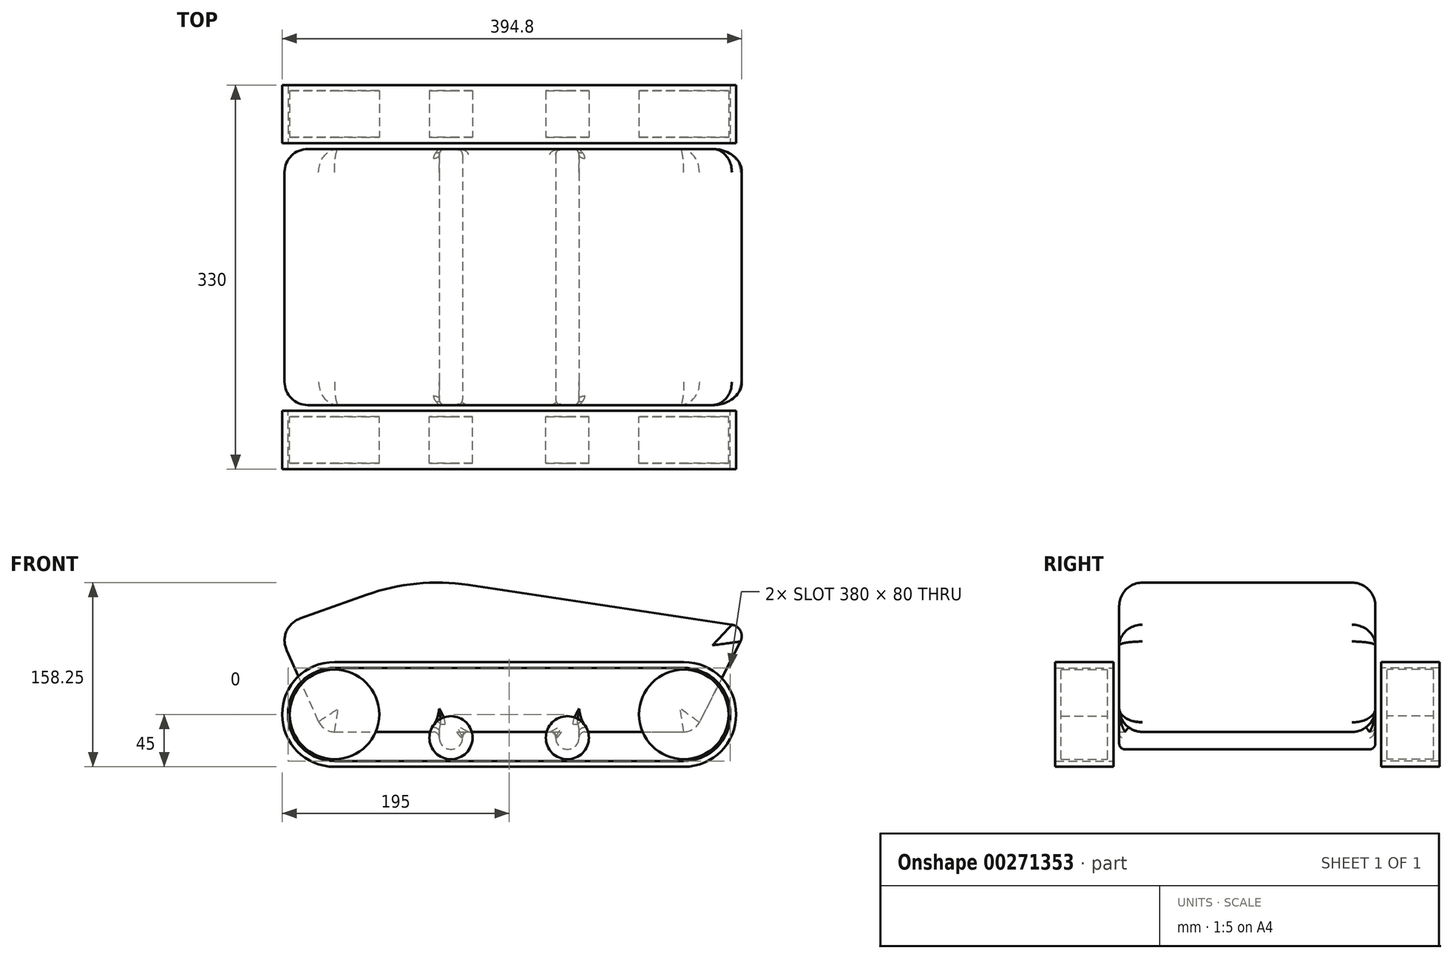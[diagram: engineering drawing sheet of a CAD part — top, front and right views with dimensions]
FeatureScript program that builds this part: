
annotation { "Feature Type Name" : "Feature", "Feature Type Description" : "" }
export const myFeature = defineFeature(function(context is Context, id is Id, definition is map)
    precondition{}
    {
        {
            var Q0;
            Q0=qCreatedBy(makeId("Front.planeOp"),FACE);
            var sketch = newSketch(context, id + "F0", { "sketchPlane" : qUnion([Q0])});
            skCircle(sketch, "E0", {"center": v(-150, 0) * mm, "radius": 40 * mm, "construction": true});
            skCircle(sketch, "E1", {"center": v(150, 0) * mm, "radius": 40 * mm, "construction": true});
            skCircle(sketch, "E2", {"center": v(-50, -20) * mm, "radius": 20 * mm, "construction": true});
            skCircle(sketch, "E3", {"center": v(50, -20) * mm, "radius": 20 * mm, "construction": true});
            skLineSegment(sketch, "E4", {"start": v(-150, -40) * mm, "end": v(150, -40) * mm});
            skLineSegment(sketch, "E5", {"start": v(150, 40) * mm, "end": v(-150, 40) * mm});
            skLineSegment(sketch, "E6.0", {"start": v(150, 45) * mm, "end": v(-150, 45) * mm});
            skLineSegment(sketch, "E7.0", {"start": v(-150, -45) * mm, "end": v(150, -45) * mm});
            skArc(sketch, "E8.0", {"start": v(-150, 45) * mm, "mid": v(-195, 0) * mm, "end": v(-150, -45) * mm});
            skArc(sketch, "E9.0", {"start": v(150, -45) * mm, "mid": v(195, 0) * mm, "end": v(150, 45) * mm});
            skCircle(sketch, "E10.0", {"center": v(-150, 0) * mm, "radius": 38.5 * mm});
            skCircle(sketch, "E11.0", {"center": v(150, 0) * mm, "radius": 38.5 * mm});
            skCircle(sketch, "E12.0", {"center": v(-50, -20) * mm, "radius": 18.5 * mm});
            skCircle(sketch, "E13.0", {"center": v(50, -20) * mm, "radius": 18.5 * mm});
            skArc(sketch, "E14", {"start": v(-150, 40) * mm, "mid": v(-190, 0) * mm, "end": v(-150, -40) * mm});
            skArc(sketch, "E15", {"start": v(150, -40) * mm, "mid": v(190, 0) * mm, "end": v(150, 40) * mm});
            skSolve(sketch);
        }
        {
            var Q0;
            Q0=makeQuery(id+"F0.imprint","IMPRINT",FACE,{"disambiguationData":[TD([[makeQuery(id+"F0.imprint","IMPRINT",EDGE,{"derivedFrom":sQuery(id+"F0.wireOp",EDGE,"E10.0")}),1.0]])]});
            var Q1;
            Q1=makeQuery(id+"F0.imprint","IMPRINT",FACE,{"disambiguationData":[TD([[makeQuery(id+"F0.imprint","IMPRINT",EDGE,{"derivedFrom":sQuery(id+"F0.wireOp",EDGE,"E11.0")}),1.0]])]});
            var Q2;
            Q2=makeQuery(id+"F0.imprint","IMPRINT",FACE,{"disambiguationData":[TD([[makeQuery(id+"F0.imprint","IMPRINT",EDGE,{"derivedFrom":sQuery(id+"F0.wireOp",EDGE,"E13.0")}),1.0]])]});
            var Q3;
            Q3=makeQuery(id+"F0.imprint","IMPRINT",FACE,{"disambiguationData":[TD([[makeQuery(id+"F0.imprint","IMPRINT",EDGE,{"derivedFrom":sQuery(id+"F0.wireOp",EDGE,"E12.0")}),1.0]])]});
            extrude(context, id + "F1", {"entities" : qUnion([Q0, Q1, Q2, Q3]), "depth" : 40 * mm});
        }
        {
            var Q0;
            Q0=makeQuery(id+"F0.imprint","IMPRINT",FACE,{"disambiguationData":[TD([[makeQuery(id+"F0.imprint","IMPRINT",EDGE,{"derivedFrom":sQuery(id+"F0.wireOp",EDGE,"E4")}),-1.0]])]});
            extrude(context, id + "F2", {"entities" : qUnion([Q0]), "depth" : 45 * mm, "hasSecondDirection" : true, "secondDirectionOppositeDirection" : true, "secondDirectionDepth" : 5 * mm});
        }
        {
            var Q0;
            Q0=qCreatedBy(makeId("Front.planeOp"),FACE);
            cPlane(context, id + "F3", {"entities" : qUnion([Q0]), "cplaneType" : CPlaneType.OFFSET, "offset" : 10 * mm, "oppositeDirection" : true, "width" : 150 * mm, "height" : 150 * mm});
        }
        {
            var Q0;
            Q0=qCreatedBy(id+"F3.planeOp",FACE);
            var sketch = newSketch(context, id + "F4", { "sketchPlane" : qUnion([Q0])});
            skPoint(sketch, "E16.0", {"position": v(-150, 0) * mm});
            skPoint(sketch, "E17.0", {"position": v(150, 0) * mm});
            skLineSegment(sketch, "E18", {"start": v(-150, -15) * mm, "end": v(-60, -15) * mm});
            skArc(sketch, "E19", {"start": v(-163.7, -6.13) * mm, "mid": v(-158.16, -12.59) * mm, "end": v(-150, -15) * mm});
            skArc(sketch, "E20", {"start": v(150, -15) * mm, "mid": v(157.84, -12.79) * mm, "end": v(163.37, -6.8) * mm});
            skPoint(sketch, "E21.0", {"position": v(-50, -20) * mm});
            skPoint(sketch, "E22.0", {"position": v(50, -20) * mm});
            skArc(sketch, "E23", {"start": v(-60, -20) * mm, "mid": v(-50, -30) * mm, "end": v(-40, -20) * mm});
            skArc(sketch, "E24", {"start": v(40, -20) * mm, "mid": v(50, -30) * mm, "end": v(60, -20) * mm});
            skLineSegment(sketch, "E25", {"start": v(-60, -20) * mm, "end": v(-60, -15) * mm});
            skLineSegment(sketch, "E26", {"start": v(-40, -20) * mm, "end": v(-40, -15) * mm});
            skLineSegment(sketch, "E27.trimOffspring", {"start": v(-40, -15) * mm, "end": v(40, -15) * mm});
            skLineSegment(sketch, "E28", {"start": v(40, -20) * mm, "end": v(40, -15) * mm});
            skLineSegment(sketch, "E29", {"start": v(60, -20) * mm, "end": v(60, -15) * mm});
            skLineSegment(sketch, "E30.trimOffspring", {"start": v(60, -15) * mm, "end": v(150, -15) * mm});
            skLineSegment(sketch, "E31", {"start": v(-163.7, -6.13) * mm, "end": v(-200, 75) * mm});
            skLineSegment(sketch, "E32", {"start": v(-200, 75) * mm, "end": v(-80, 118) * mm});
            skLineSegment(sketch, "E33", {"start": v(-80, 118) * mm, "end": v(205, 75) * mm});
            skLineSegment(sketch, "E34", {"start": v(205, 75) * mm, "end": v(163.37, -6.8) * mm});
            skSolve(sketch);
        }
        {
            var Q0;
            Q0=makeQuery(id+"F4.imprint","IMPRINT",FACE,{"disambiguationData":[TD([[makeQuery(id+"F4.imprint","IMPRINT",EDGE,{"derivedFrom":sQuery(id+"F4.wireOp",EDGE,"E18")}),1.0]])]});
            extrude(context, id + "F5", {"entities" : qUnion([Q0]), "oppositeDirection" : true, "depth" : 220 * mm});
        }
        {
            var Q0;
            Q0=makeQuery(id+"F5.opExtrude","SWEPT_EDGE",EDGE,{"disambiguationData":[OSD([sQuery(id+"F4.wireOp",EDGE,"E31"),sQuery(id+"F4.wireOp",EDGE,"E32")])]});
            fillet(context, id + "F6", {"entities" : qUnion([Q0]), "radius" : 20 * mm, "tangentPropagation" : true, "allowEdgeOverflow" : false});
        }
        {
            var Q0;
            Q0=makeQuery(id+"F5.opExtrude","SWEPT_EDGE",EDGE,{"disambiguationData":[OSD([sQuery(id+"F4.wireOp",EDGE,"E32"),sQuery(id+"F4.wireOp",EDGE,"E33")])]});
            fillet(context, id + "F7", {"entities" : qUnion([Q0]), "radius" : 180 * mm, "tangentPropagation" : true, "allowEdgeOverflow" : false});
        }
        {
            var Q0;
            Q0=makeQuery(id+"F5.opExtrude","SWEPT_EDGE",EDGE,{"disambiguationData":[OSD([sQuery(id+"F4.wireOp",EDGE,"E33"),sQuery(id+"F4.wireOp",EDGE,"E34")])]});
            fillet(context, id + "F8", {"entities" : qUnion([Q0]), "radius" : 10 * mm, "tangentPropagation" : true, "allowEdgeOverflow" : false});
        }
        {
            var Q0;
            Q0=makeQuery(id+"F5.opExtrude","CAP_FACE",FACE,{"disambiguationData":[OSD([sQuery(id+"F4.wireOp",EDGE,"E18"),sQuery(id+"F4.wireOp",EDGE,"E19"),sQuery(id+"F4.wireOp",EDGE,"E20"),sQuery(id+"F4.wireOp",EDGE,"E23"),sQuery(id+"F4.wireOp",EDGE,"E24"),sQuery(id+"F4.wireOp",EDGE,"E25"),sQuery(id+"F4.wireOp",EDGE,"E26"),sQuery(id+"F4.wireOp",EDGE,"E27.trimOffspring"),sQuery(id+"F4.wireOp",EDGE,"E28"),sQuery(id+"F4.wireOp",EDGE,"E29"),sQuery(id+"F4.wireOp",EDGE,"E30.trimOffspring"),sQuery(id+"F4.wireOp",EDGE,"E31"),sQuery(id+"F4.wireOp",EDGE,"E32"),sQuery(id+"F4.wireOp",EDGE,"E33"),sQuery(id+"F4.wireOp",EDGE,"E34")])],"isStart":true});
            cPlane(context, id + "F9", {"entities" : qUnion([Q0]), "cplaneType" : CPlaneType.OFFSET, "offset" : 110 * mm, "oppositeDirection" : true, "width" : 150 * mm, "height" : 150 * mm});
        }
        {
            var Q0;
            Q0=makeQuery(id+"F1.opExtrude","SWEPT_BODY",BODY,{"disambiguationData":[OSD([sQuery(id+"F0.wireOp",EDGE,"E10.0")])]});
            var Q1;
            Q1=makeQuery(id+"F1.opExtrude","SWEPT_BODY",BODY,{"disambiguationData":[OSD([sQuery(id+"F0.wireOp",EDGE,"E12.0")])]});
            var Q2;
            Q2=makeQuery(id+"F1.opExtrude","SWEPT_BODY",BODY,{"disambiguationData":[OSD([sQuery(id+"F0.wireOp",EDGE,"E13.0")])]});
            var Q3;
            Q3=makeQuery(id+"F1.opExtrude","SWEPT_BODY",BODY,{"disambiguationData":[OSD([sQuery(id+"F0.wireOp",EDGE,"E11.0")])]});
            var Q4;
            Q4=makeQuery(id+"F2.opExtrude","SWEPT_BODY",BODY,{"disambiguationData":[OSD([sQuery(id+"F0.wireOp",EDGE,"E4"),sQuery(id+"F0.wireOp",EDGE,"E5"),sQuery(id+"F0.wireOp",EDGE,"E6.0"),sQuery(id+"F0.wireOp",EDGE,"E7.0"),sQuery(id+"F0.wireOp",EDGE,"E8.0"),sQuery(id+"F0.wireOp",EDGE,"E9.0"),sQuery(id+"F0.wireOp",EDGE,"E14"),sQuery(id+"F0.wireOp",EDGE,"E15")])]});
            var Q5;
            Q5=qCreatedBy(id+"F9.planeOp",FACE);
            mirror(context, id + "F10", {"entities" : qUnion([Q0, Q1, Q2, Q3, Q4]), "mirrorPlane" : qUnion([Q5])});
        }
        {
            var Q0;
            {var subQ0=sQuery(id+"F4.wireOp",EDGE,"E33");var subQ1=sQuery(id+"F4.wireOp",EDGE,"E32");Q0=makeQuery(id+"F7.opFillet","BLEND_EDGE",EDGE,{"blendedFrom":[makeQuery(id+"F5.opExtrude","SWEPT_EDGE",EDGE,{"disambiguationData":[OSD([subQ1,subQ0])]}),makeQuery(id+"F5.opExtrude","CAP_FACE",FACE,{"disambiguationData":[OSD([sQuery(id+"F4.wireOp",EDGE,"E18"),sQuery(id+"F4.wireOp",EDGE,"E19"),sQuery(id+"F4.wireOp",EDGE,"E20"),sQuery(id+"F4.wireOp",EDGE,"E23"),sQuery(id+"F4.wireOp",EDGE,"E24"),sQuery(id+"F4.wireOp",EDGE,"E25"),sQuery(id+"F4.wireOp",EDGE,"E26"),sQuery(id+"F4.wireOp",EDGE,"E27.trimOffspring"),sQuery(id+"F4.wireOp",EDGE,"E28"),sQuery(id+"F4.wireOp",EDGE,"E29"),sQuery(id+"F4.wireOp",EDGE,"E30.trimOffspring"),sQuery(id+"F4.wireOp",EDGE,"E31"),subQ1,subQ0,sQuery(id+"F4.wireOp",EDGE,"E34")])],"isStart":true})],"blendedInto":[makeQuery(id+"F5.opExtrude","CAP_FACE",FACE,{"disambiguationData":[OSD([sQuery(id+"F4.wireOp",EDGE,"E18"),sQuery(id+"F4.wireOp",EDGE,"E19"),sQuery(id+"F4.wireOp",EDGE,"E20"),sQuery(id+"F4.wireOp",EDGE,"E23"),sQuery(id+"F4.wireOp",EDGE,"E24"),sQuery(id+"F4.wireOp",EDGE,"E25"),sQuery(id+"F4.wireOp",EDGE,"E26"),sQuery(id+"F4.wireOp",EDGE,"E27.trimOffspring"),sQuery(id+"F4.wireOp",EDGE,"E28"),sQuery(id+"F4.wireOp",EDGE,"E29"),sQuery(id+"F4.wireOp",EDGE,"E30.trimOffspring"),sQuery(id+"F4.wireOp",EDGE,"E31"),subQ1,subQ0,sQuery(id+"F4.wireOp",EDGE,"E34")])],"isStart":true})]});}
            var Q1;
            Q1=makeQuery(id+"F5.opExtrude","CAP_EDGE",EDGE,{"disambiguationData":[OSD([sQuery(id+"F4.wireOp",EDGE,"E32")])],"isStart":false});
            fillet(context, id + "F11", {"entities" : qUnion([Q0, Q1]), "radius" : 20 * mm, "tangentPropagation" : true, "allowEdgeOverflow" : false});
        }
        {
            var Q0;
            Q0=makeQuery(id+"F5.opExtrude","CAP_EDGE",EDGE,{"disambiguationData":[OSD([sQuery(id+"F4.wireOp",EDGE,"E25")])],"isStart":true});
            var Q1;
            Q1=makeQuery(id+"F5.opExtrude","CAP_EDGE",EDGE,{"disambiguationData":[OSD([sQuery(id+"F4.wireOp",EDGE,"E29")])],"isStart":true});
            var Q2;
            Q2=makeQuery(id+"F5.opExtrude","CAP_FACE",FACE,{"disambiguationData":[OSD([sQuery(id+"F4.wireOp",EDGE,"E18"),sQuery(id+"F4.wireOp",EDGE,"E19"),sQuery(id+"F4.wireOp",EDGE,"E20"),sQuery(id+"F4.wireOp",EDGE,"E23"),sQuery(id+"F4.wireOp",EDGE,"E24"),sQuery(id+"F4.wireOp",EDGE,"E25"),sQuery(id+"F4.wireOp",EDGE,"E26"),sQuery(id+"F4.wireOp",EDGE,"E27.trimOffspring"),sQuery(id+"F4.wireOp",EDGE,"E28"),sQuery(id+"F4.wireOp",EDGE,"E29"),sQuery(id+"F4.wireOp",EDGE,"E30.trimOffspring"),sQuery(id+"F4.wireOp",EDGE,"E31"),sQuery(id+"F4.wireOp",EDGE,"E32"),sQuery(id+"F4.wireOp",EDGE,"E33"),sQuery(id+"F4.wireOp",EDGE,"E34")])],"isStart":false});
            fillet(context, id + "F12", {"entities" : qUnion([Q0, Q1, Q2]), "radius" : 5 * mm, "tangentPropagation" : true, "allowEdgeOverflow" : false});
        }
        {
            var Q0;
            {var subQ0=sQuery(id+"F4.wireOp",EDGE,"E30.trimOffspring");Q0=makeQuery(id+"F12.opFillet","BLEND_EDGE",EDGE,{"blendedFrom":[makeQuery(id+"F5.opExtrude","CAP_EDGE",EDGE,{"disambiguationData":[OSD([sQuery(id+"F4.wireOp",EDGE,"E29")])],"isStart":false}),makeQuery(id+"F11.opFillet","BLEND_FACE",FACE,{"disambiguationData":[OSD([subQ0]),TDD([makeQuery(id+"F5.opExtrude","CAP_EDGE",EDGE,{"disambiguationData":[OSD([subQ0])],"isStart":false})])]})],"blendedInto":[makeQuery(id+"F11.opFillet","BLEND_FACE",FACE,{"disambiguationData":[OSD([subQ0]),TDD([makeQuery(id+"F5.opExtrude","CAP_EDGE",EDGE,{"disambiguationData":[OSD([subQ0])],"isStart":false})])]})]});}
            var Q1;
            {var subQ0=sQuery(id+"F4.wireOp",EDGE,"E18");Q1=makeQuery(id+"F12.opFillet","BLEND_EDGE",EDGE,{"blendedFrom":[makeQuery(id+"F5.opExtrude","CAP_EDGE",EDGE,{"disambiguationData":[OSD([sQuery(id+"F4.wireOp",EDGE,"E25")])],"isStart":false}),makeQuery(id+"F11.opFillet","BLEND_FACE",FACE,{"disambiguationData":[OSD([subQ0]),TDD([makeQuery(id+"F5.opExtrude","CAP_EDGE",EDGE,{"disambiguationData":[OSD([subQ0])],"isStart":false})])]})],"blendedInto":[makeQuery(id+"F11.opFillet","BLEND_FACE",FACE,{"disambiguationData":[OSD([subQ0]),TDD([makeQuery(id+"F5.opExtrude","CAP_EDGE",EDGE,{"disambiguationData":[OSD([subQ0])],"isStart":false})])]})]});}
            fillet(context, id + "F13", {"entities" : qUnion([Q0, Q1]), "radius" : 5 * mm, "tangentPropagation" : true, "allowEdgeOverflow" : false});
        }
        {
            var Q0;
            Q0=makeQuery(id+"F5.opExtrude","SWEPT_EDGE",EDGE,{"disambiguationData":[OSD([sQuery(id+"F4.wireOp",EDGE,"E26"),sQuery(id+"F4.wireOp",EDGE,"E27.trimOffspring")])]});
            var Q1;
            Q1=makeQuery(id+"F5.opExtrude","SWEPT_EDGE",EDGE,{"disambiguationData":[OSD([sQuery(id+"F4.wireOp",EDGE,"E27.trimOffspring"),sQuery(id+"F4.wireOp",EDGE,"E28")])]});
            fillet(context, id + "F14", {"entities" : qUnion([Q0, Q1]), "radius" : 5 * mm, "tangentPropagation" : true, "allowEdgeOverflow" : false});
        }
    });
